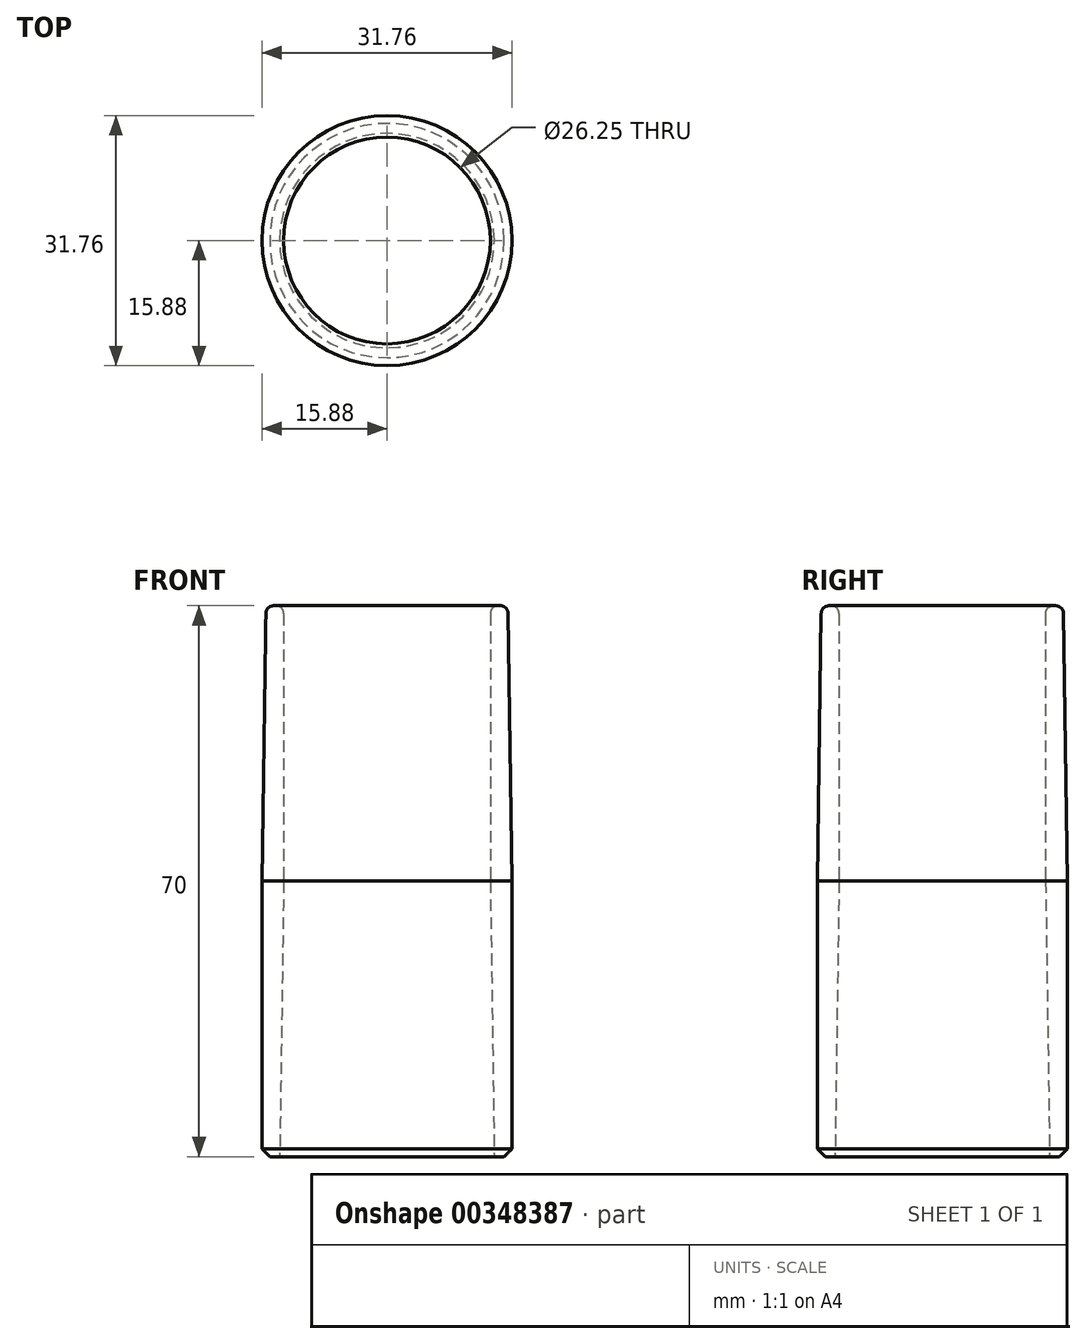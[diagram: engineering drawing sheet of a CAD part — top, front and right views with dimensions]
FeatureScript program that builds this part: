
annotation { "Feature Type Name" : "Feature", "Feature Type Description" : "" }
export const myFeature = defineFeature(function(context is Context, id is Id, definition is map)
    precondition{}
    {
        {
            var Q0;
            Q0=qCreatedBy(makeId("Front.planeOp"),FACE);
            var sketch = newSketch(context, id + "F0", { "sketchPlane" : qUnion([Q0])});
            skLineSegment(sketch, "E0", {"start": v(15.88, 35) * mm, "end": v(15.88, 0) * mm});
            skLineSegment(sketch, "E1", {"start": v(15.88, 0) * mm, "end": v(13.62, 0) * mm});
            skLineSegment(sketch, "E2", {"start": v(0, -17.76) * mm, "end": v(0, 76.68) * mm, "construction": true});
            skPoint(sketch, "E3.end.orphan", {"position": v(15.62, 35) * mm});
            skLineSegment(sketch, "E4", {"start": v(40.05, 35) * mm, "end": v(-27.3, 35) * mm, "construction": true});
            skLineSegment(sketch, "E5", {"start": v(13.62, 0) * mm, "end": v(13.12, 35) * mm});
            skLineSegment(sketch, "E6", {"start": v(-27.55, 70) * mm, "end": v(32.72, 70) * mm, "construction": true});
            skLineSegment(sketch, "E7", {"start": v(13.12, 35) * mm, "end": v(13.12, 70) * mm});
            skLineSegment(sketch, "E8", {"start": v(15.88, 35) * mm, "end": v(15.38, 70) * mm});
            skLineSegment(sketch, "E9", {"start": v(15.38, 70) * mm, "end": v(13.12, 70) * mm});
            skSolve(sketch);
        }
        {
            var Q0;
            Q0=makeQuery(id+"F0.imprint","IMPRINT",FACE,{"disambiguationData":[TD([[makeQuery(id+"F0.imprint","IMPRINT",EDGE,{"derivedFrom":sQuery(id+"F0.wireOp",EDGE,"E0")}),-1.0]])]});
            var Q1;
            Q1=sQuery(id+"F0.wireOp",EDGE,"E2");
            revolve(context, id + "F1", {"entities" : qUnion([Q0]), "axis" : qUnion([Q1]), "revolveType" : RevolveType.FULL});
        }
        {
            var Q0;
            Q0=makeQuery(id+"F1.opRevolve","SWEPT_EDGE",EDGE,{"disambiguationData":[OSD([sQuery(id+"F0.wireOp",EDGE,"E8"),sQuery(id+"F0.wireOp",EDGE,"E9")])]});
            var Q1;
            Q1=makeQuery(id+"F1.opRevolve","SWEPT_EDGE",EDGE,{"disambiguationData":[OSD([sQuery(id+"F0.wireOp",EDGE,"E7"),sQuery(id+"F0.wireOp",EDGE,"E9")])]});
            fillet(context, id + "F2", {"entities" : qUnion([Q0, Q1]), "radius" : 1 * mm, "tangentPropagation" : true, "allowEdgeOverflow" : false});
        }
        {
            var Q0;
            Q0=makeQuery(id+"F1.opRevolve","SWEPT_EDGE",EDGE,{"disambiguationData":[OSD([sQuery(id+"F0.wireOp",EDGE,"E0"),sQuery(id+"F0.wireOp",EDGE,"E1")])]});
            chamfer(context, id + "F3", {"entities" : qUnion([Q0]), "width" : 1 * mm, "tangentPropagation" : true});
        }
    });
